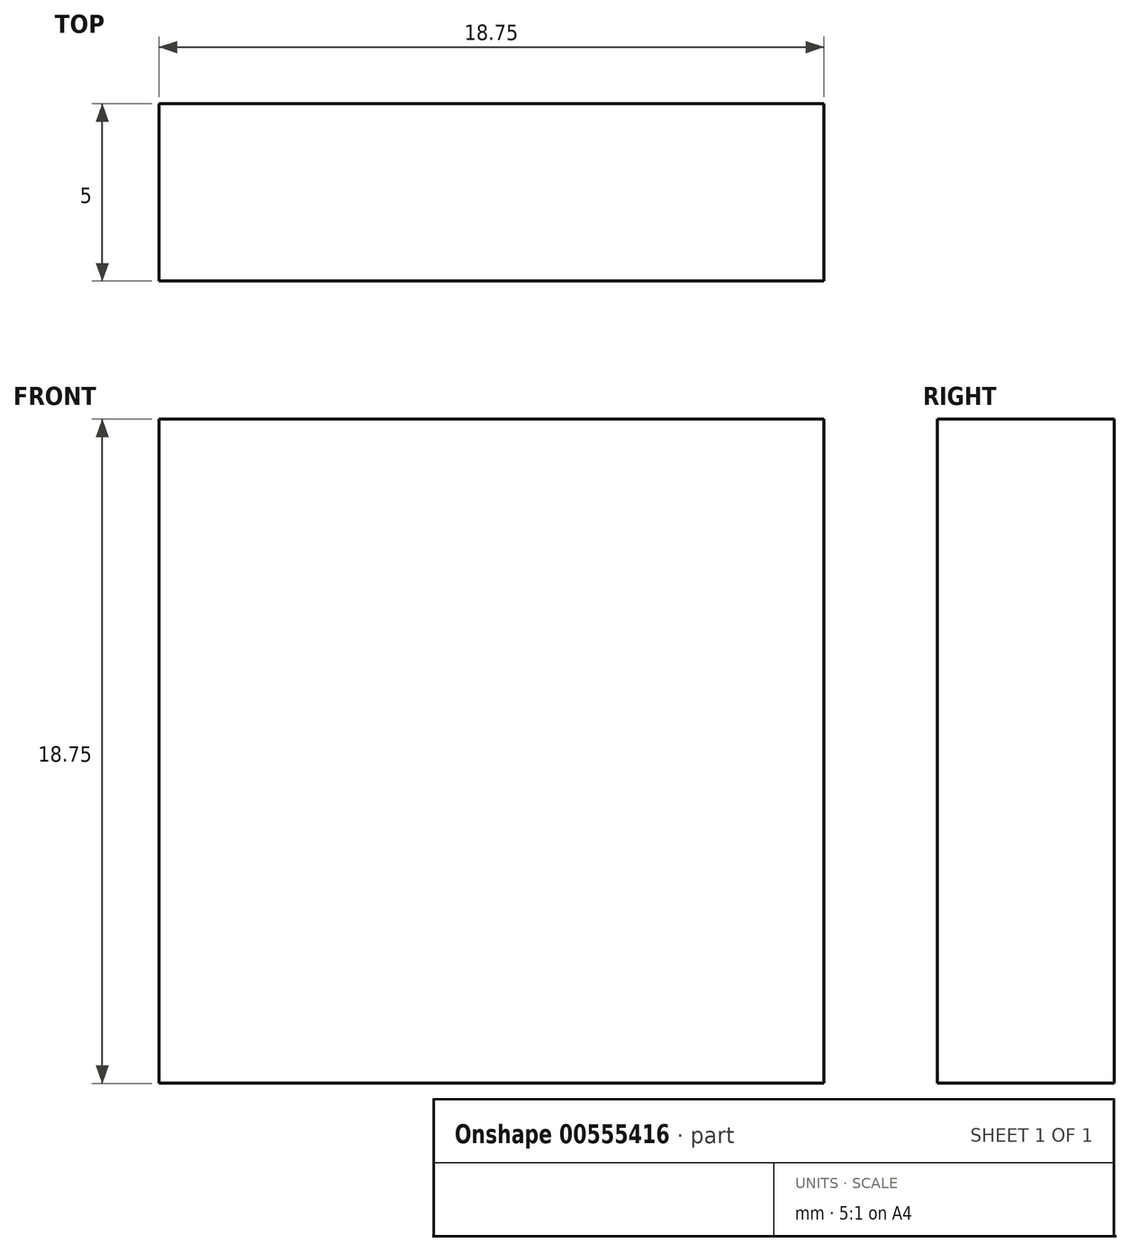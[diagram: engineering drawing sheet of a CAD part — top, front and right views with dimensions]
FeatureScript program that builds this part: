
annotation { "Feature Type Name" : "Feature", "Feature Type Description" : "" }
export const myFeature = defineFeature(function(context is Context, id is Id, definition is map)
    precondition{}
    {
        {
            var Q0;
            Q0=qCreatedBy(makeId("Front.planeOp"),FACE);
            var sketch = newSketch(context, id + "F0", { "sketchPlane" : qUnion([Q0])});
            skLineSegment(sketch, "E0.bottom", {"start": v(-164.06, 86.11) * mm, "end": v(-145.3, 86.11) * mm});
            skLineSegment(sketch, "E0.top", {"start": v(-164.06, 67.36) * mm, "end": v(-145.3, 67.36) * mm});
            skLineSegment(sketch, "E0.left", {"start": v(-164.06, 86.11) * mm, "end": v(-164.06, 67.36) * mm});
            skLineSegment(sketch, "E0.right", {"start": v(-145.3, 86.11) * mm, "end": v(-145.3, 67.36) * mm});
            skSolve(sketch);
        }
        {
            var Q0;
            Q0=makeQuery(id+"F0.imprint","IMPRINT",FACE,{"disambiguationData":[TD([[makeQuery(id+"F0.imprint","IMPRINT",EDGE,{"derivedFrom":sQuery(id+"F0.wireOp",EDGE,"E0.bottom")}),-1.0]])]});
            extrude(context, id + "F1", {"entities" : qUnion([Q0]), "depth" : 5 * mm, "offsetDistance" : 25 * mm});
        }
    });
